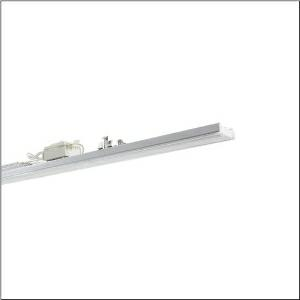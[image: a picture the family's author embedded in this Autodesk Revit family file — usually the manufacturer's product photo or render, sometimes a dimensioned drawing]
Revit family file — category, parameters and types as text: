
# Revit family: licross_11_recessed_ho_51te12dn4exm
name_source: partatom
category: Lighting Fixtures
units: mm (PartAtom-declared; Revit-internal decimal feet)

## family parameters
Cut with Voids When Loaded = No
Host = Face
Light Source = No
Part Type = Normal
Room Calculation Point = No
Round Connector Dimension = Use Diameter
Shared = No

## types (1)
- --- (1 x LED, 14030 lm, 76.8 W, 4000K)
    Apparent Load = 77 VA
    CIE Flux Codes = 66 91 98 100 100
    Color Rendering = 80
    Color Temperature = 4000K
    Default Elevation = 1800 mm
    Description = Licross 11 Recessed HO, luminaire insert, of sheet steel, galvanised, coil coated, white, length: 1.500mm, width: 66mm, height: 67mm, LED rated luminous flux: 14.030lm, light colour: 840, SDCM (Standard Deviation of Colour Matching)MacAdam ≤ 2 SDCM (initial), control gear: DALI 2, with plug, 5-pole, with phase selection, mains connection: 220..240V, AC, 50/60Hz, rated input power: 77W, internal wiring halogen-free, primary optical cover: cover, of PMMA, light emission: direct distribution, primary light characteristic: symmetric, protection rating (complete): IP54, insulation class (complete): insulation class I (protective earthing), certification: CE, ENEC, VDE, UKCA, protection symbol: D if used in an environment with non-conductive dust loads with corresponding accessories, impact resistance: IK06, permissible ambient temperature for indoor applications: -25..+30°C, corresponds to IFS (International Featured Standards) requirements for safety and quality in the food industry, reducing of maximum allowable ambient temperature of 5°C with ceiling mounting, LABS conformity tested according to VDMA 24364:2018-05, The light source and the operating device comply with the requirements of the Ecodesign Regulation (EU) 2019/2020 and are replaceable in accordance with this regulation, packaging unit: 1 piece
    Height = 58 mm
    Lamp = 1 x LED
    Lamp Light Flux = 14030 lm
    Lamp Power = 76.8 W
    Lamp count = 1
    Length = 1500 mm
    Luminous efficacy = 183 lm/W
    Manufacturer = Siteco
    ModVariant = No
    Model = 51TE12DN4EXM
    Mounting Place = Ceiling
    Mounting Type = Pendant
    Number of Poles = 1
    OnlyDefault = Yes
    Power Factor = 1
    Product Name = Licross 11 Recessed HO
    Product group = luminaire insert | ceiling pendant
    ProductGroupID = 901
    Protection Class = Protection class I
    Protection Degree = IP 54
    RLX_Detail_Level = 1
    RLX_Emergency_Light_Flux = 0 lm
    RLX_Emergency_Type = 0
    RLX_Emergency_Type_DB = No
    RlxData = <blob elided: 24933 chars, md5=8a9669ba>
    Socket = socket
    Standby Power = 0 W
    System Light Flux = 14030 lm
    System Power = 77 W
    Type Comments = factory setting: luminous flux: 100 % | dim-lin: 254 | 522 mA
    Type Image = l_1296930.jpg
    URL = http://relux.com
    VarID = @adj_101109
    Voltage = 0 V
    Weight = 0.00 kg
    Width = 66 mm

## geometry (parser evidence)
native form markers: Blend x4, Sweep x12
no freeform markers — native parametric forms only
